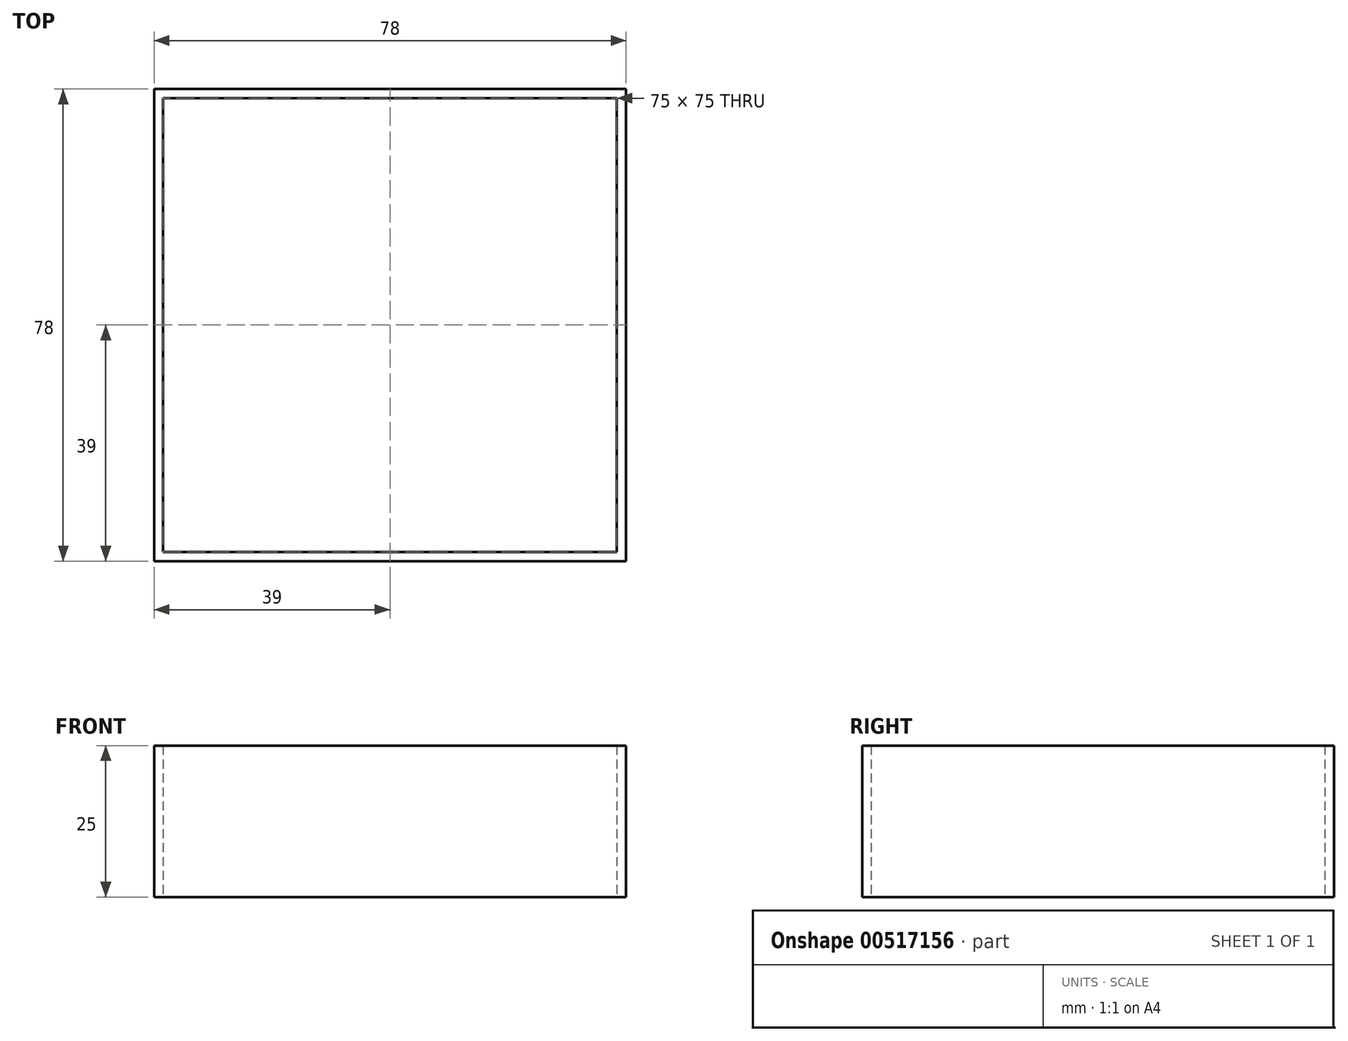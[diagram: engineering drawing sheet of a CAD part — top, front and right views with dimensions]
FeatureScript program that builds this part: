
annotation { "Feature Type Name" : "Feature", "Feature Type Description" : "" }
export const myFeature = defineFeature(function(context is Context, id is Id, definition is map)
    precondition{}
    {
        {
            var Q0;
            Q0=qCreatedBy(makeId("Top.planeOp"),FACE);
            var sketch = newSketch(context, id + "F0", { "sketchPlane" : qUnion([Q0])});
            skLineSegment(sketch, "E0.bottom", {"start": v(-37.5, 37.5) * mm, "end": v(37.5, 37.5) * mm});
            skLineSegment(sketch, "E0.top", {"start": v(-37.5, -37.5) * mm, "end": v(37.5, -37.5) * mm});
            skLineSegment(sketch, "E0.left", {"start": v(-37.5, 37.5) * mm, "end": v(-37.5, -37.5) * mm});
            skLineSegment(sketch, "E0.right", {"start": v(37.5, 37.5) * mm, "end": v(37.5, -37.5) * mm});
            skPoint(sketch, "E0.middle", {"position": v(0, 0) * mm});
            skLineSegment(sketch, "E1.bottom", {"start": v(39, -39) * mm, "end": v(-39, -39) * mm});
            skLineSegment(sketch, "E1.top", {"start": v(39, 39) * mm, "end": v(-39, 39) * mm});
            skLineSegment(sketch, "E1.left", {"start": v(39, -39) * mm, "end": v(39, 39) * mm});
            skLineSegment(sketch, "E1.right", {"start": v(-39, -39) * mm, "end": v(-39, 39) * mm});
            skSolve(sketch);
        }
        {
            var Q0;
            Q0 = qSketchRegion(id + "F0", true);
            extrude(context, id + "F1", {"entities" : qUnion([Q0]), "depth" : 25 * mm, "offsetDistance" : 25 * mm});
        }
    });
